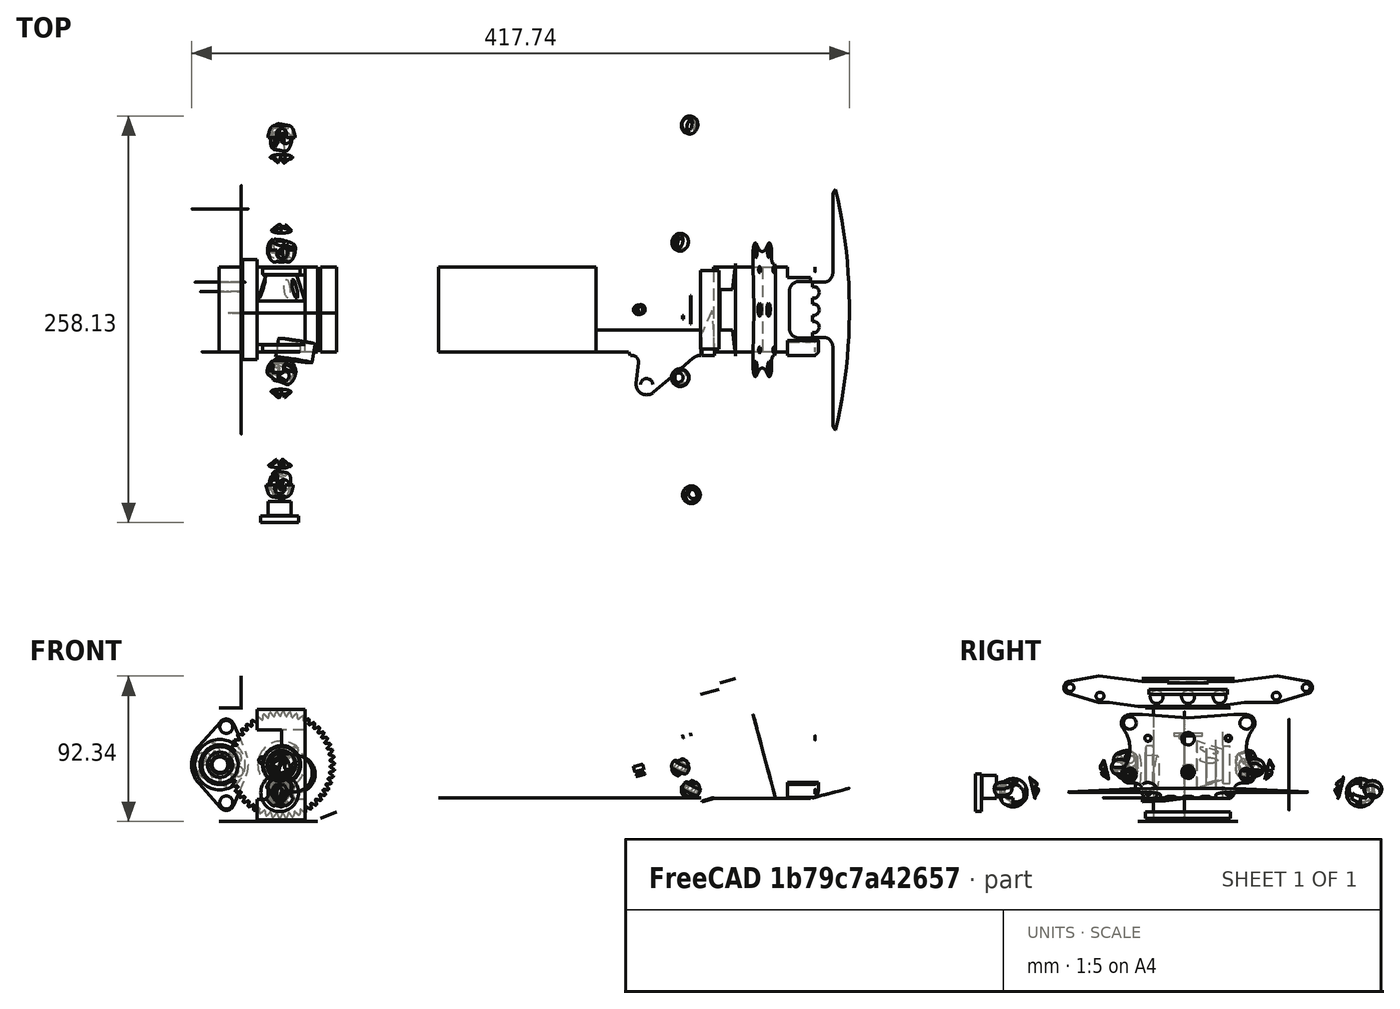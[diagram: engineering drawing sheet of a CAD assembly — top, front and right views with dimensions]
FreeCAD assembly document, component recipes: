
FREECAD ASSEMBLY — COMPONENT RECIPES ("Tarmo5")

This assembly document has 7 components, labeled P0..P6 below (a component is one placed body or linked part). 5 of them carry a construction recipe — the FreeCAD feature program that regenerates the part from scratch, quoted from this document or its linked companion documents; the rest are supplied as boundary geometry only. No exploded tour is included for this assembly.
COMPONENT P0 — geometry summary ("M4x16-Screw"; no construction recipe available for this part):
  bounding box: 239.9 x 42.7 x 19.5 mm
  tessellated surface: 19,088 triangles
  volume: 1333 mm^3 (1% of its bounding box)
  symmetry: mirror-symmetric across its y mid-plane
COMPONENT P1 — recipe-attached ("Link080(M4x35-Screw)", a linked part whose construction recipe lives in a companion FreeCAD document of the same project; that document's serialized recipe follows).
Construction recipe (the companion document, serialized — sketch geometry with constraints, then the solid features built on it; lengths are millimeters unless a unit is written):

FCSTD DOCUMENT  (FreeCAD 2022.1021R26244 +5249 (Git))
Label: M4x35Screws
License: All rights reserved
LicenseURL: http://en.wikipedia.org/wiki/All_rights_reserved
objects: Part::FeaturePython×1
note: 1 computed .brp shape members not serialized (recipe doc carries the construction recipe); baked Part::Feature solids carry a one-line shape summary decoded from their .brp

FEATURE [Part::FeaturePython] Screw  label="M4x35-Screw"  # Fasteners workbench fastener (typed FeaturePython)
  TreeRank = 1
  diameter = 5
  invert = false
  leftHanded = false
  length = 9
  lengthCustom = 35
  matchOuter = false
  offset = 0
  thread = false
  type = 45
COMPONENT P2 — recipe-attached ("Link081(M4x45-Screw)", a linked part whose construction recipe lives in a companion FreeCAD document of the same project; that document's serialized recipe follows).
Construction recipe (the companion document, serialized — sketch geometry with constraints, then the solid features built on it; lengths are millimeters unless a unit is written):

FCSTD DOCUMENT  (FreeCAD 2022.1021R26244 +5249 (Git))
Label: M4x45Screws
License: All rights reserved
LicenseURL: http://en.wikipedia.org/wiki/All_rights_reserved
objects: Part::FeaturePython×1
note: 1 computed .brp shape members not serialized (recipe doc carries the construction recipe); baked Part::Feature solids carry a one-line shape summary decoded from their .brp

FEATURE [Part::FeaturePython] Screw  label="M4x50-Screw"  # Fasteners workbench fastener (typed FeaturePython)
  TreeRank = 1
  diameter = 5
  invert = false
  leftHanded = false
  length = 11
  lengthCustom = 50
  matchOuter = false
  offset = 0
  thread = false
  type = 45
COMPONENT P3 — geometry summary ("Link082(M4x50-Screw)"; no construction recipe available for this part):
  bounding box: 85.0 x 54.0 x 41.0 mm
  tessellated surface: 19,768 triangles
  volume: 3042 mm^3 (2% of its bounding box)
  symmetry: 2-fold rotationally symmetric about the x axis; mirror-symmetric across its y mid-plane, z mid-plane
COMPONENT P4 — recipe-attached ("Link083(M4x16-Screw)", a linked part whose construction recipe lives in a companion FreeCAD document of the same project; that document's serialized recipe follows).
Construction recipe (the companion document, serialized — sketch geometry with constraints, then the solid features built on it; lengths are millimeters unless a unit is written):

FCSTD DOCUMENT  (FreeCAD 2022.1021R26244 +5249 (Git))
Label: M4x16Screws
License: All rights reserved
LicenseURL: http://en.wikipedia.org/wiki/All_rights_reserved
objects: Part::FeaturePython×1, App::Link×1
note: 1 computed .brp shape members not serialized (recipe doc carries the construction recipe); baked Part::Feature solids carry a one-line shape summary decoded from their .brp

FEATURE [Part::FeaturePython] Screw  label="M4x16-Screw"  # Fasteners workbench fastener (typed FeaturePython)
  TreeRank = 1
  diameter = 5
  invert = false
  leftHanded = false
  length = 5
  lengthCustom = 16
  matchOuter = false
  offset = 0
  thread = false
  type = 45
FEATURE [App::Link] Link  label="Link(M4x16-Screw)"
  AutoLinkLabel = true
  AutoPlacement = true
  LinkedObject = -> Screw
  SyncGroupVisibility = false
  TreeRank = 2
  _LinkVersion = 1
COMPONENT P5 — same part as P4; its construction recipe is shown at P4.
COMPONENT P6 — recipe-attached ("Link085(M3-Nut)", a linked part whose construction recipe lives in a companion FreeCAD document of the same project; that document's serialized recipe follows).
Construction recipe (the companion document, serialized — sketch geometry with constraints, then the solid features built on it; lengths are millimeters unless a unit is written):

FCSTD DOCUMENT  (FreeCAD 2022.1021R26244 +5249 (Git))
Label: M3_Nut
License: All rights reserved
LicenseURL: http://en.wikipedia.org/wiki/All_rights_reserved
objects: Part::FeaturePython×1
note: 1 computed .brp shape members not serialized (recipe doc carries the construction recipe); baked Part::Feature solids carry a one-line shape summary decoded from their .brp

FEATURE [Part::FeaturePython] Nut  label="M3-Nut"  # Fasteners workbench fastener (typed FeaturePython)
  TreeRank = 1
  diameter = 4
  invert = false
  leftHanded = false
  matchOuter = false
  offset = 0
  thread = false
  type = 22
PROVENANCE & LICENSES
A FreeCAD (.FCStd) document from a public repository crawl; recipes are the document's own serialized feature recipes (and, for linked parts, companion documents' recipes).
License: as declared in the source repository (recorded in the dataset sidecar).
